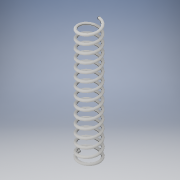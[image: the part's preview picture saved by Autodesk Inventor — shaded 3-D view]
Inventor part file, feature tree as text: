
AUTODESK INVENTOR PART (.ipt)
format: ipt  version: 2018 (Build 220112000, 112)  size: 408,576 bytes
history: native  units: in
note: dims shown in document units (in); Inventor stores cm internally (conversion verified against a paired STEP export)
features: helix x1, sketch x1
ambient origin geometry x8: Origin, YZ Plane, XZ Plane, XY Plane, X Axis, Y Axis, Z Axis, Center Point
bodies: Solid1 (feature_tree)
feature tree (2):
  helix  "Coil1"  [1 undecoded]
  sketch  "Sketch1"  dims[d1=0.09in d2=1.0in d3=0.94in d4=5.5118in d5=0.0in d6=90.0deg d7=180.0deg d8=0.0in d9=0.0in]
note: 1 required parameter value undecoded (feature->parameter linkage not recoverable at this tier; creation-order binding heuristic only, values carry confidence <= 0.55)
